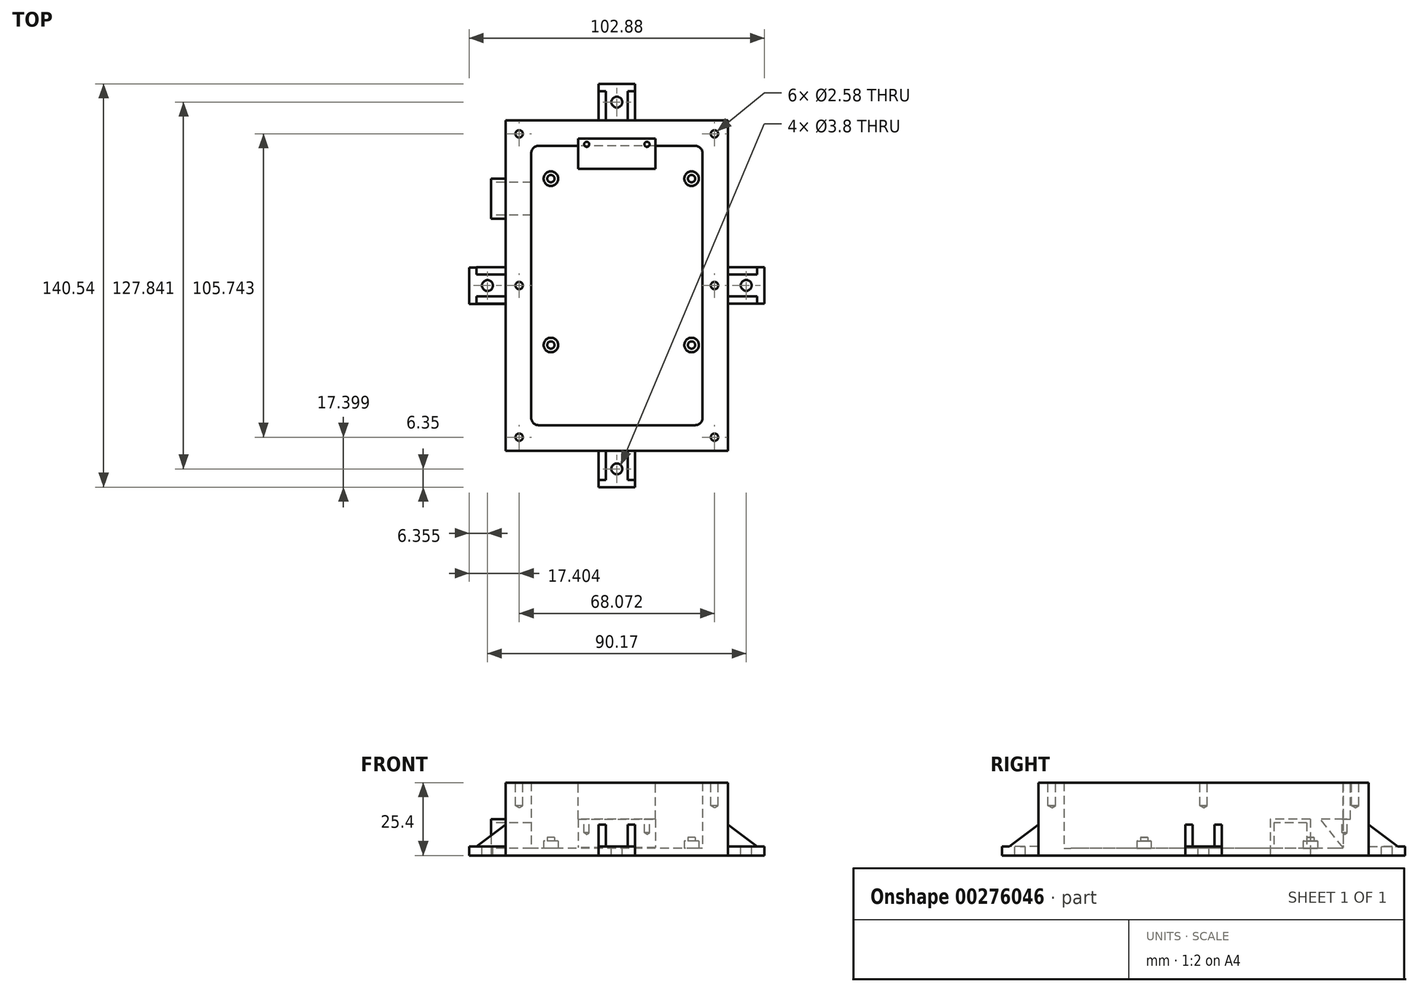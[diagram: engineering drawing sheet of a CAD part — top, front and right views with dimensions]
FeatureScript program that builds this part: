
annotation { "Feature Type Name" : "Feature", "Feature Type Description" : "" }
export const myFeature = defineFeature(function(context is Context, id is Id, definition is map)
    precondition{}
    {
        {
            var Q0;
            Q0=qCreatedBy(makeId("Top.planeOp"),FACE);
            var sketch = newSketch(context, id + "F0", { "sketchPlane" : qUnion([Q0])});
            skLineSegment(sketch, "E0.bottom", {"start": v(38.74, 57.57) * mm, "end": v(-38.74, 57.57) * mm});
            skLineSegment(sketch, "E0.top", {"start": v(38.74, -57.57) * mm, "end": v(-38.74, -57.57) * mm});
            skLineSegment(sketch, "E0.left", {"start": v(38.74, 57.57) * mm, "end": v(38.73, -57.57) * mm});
            skLineSegment(sketch, "E0.right", {"start": v(-38.73, 57.57) * mm, "end": v(-38.74, -57.57) * mm});
            skPoint(sketch, "E0.middle", {"position": v(0, 0) * mm});
            skLineSegment(sketch, "E1.bottom", {"start": v(27.3, 48.68) * mm, "end": v(-27.3, 48.68) * mm});
            skLineSegment(sketch, "E1.top", {"start": v(27.3, -48.68) * mm, "end": v(-27.3, -48.68) * mm});
            skLineSegment(sketch, "E1.left", {"start": v(29.85, 46.14) * mm, "end": v(29.84, -46.14) * mm});
            skLineSegment(sketch, "E1.right", {"start": v(-29.84, 46.14) * mm, "end": v(-29.85, -46.14) * mm});
            skPoint(sketch, "E2.visualSharp", {"position": v(-29.84, 48.68) * mm});
            skPoint(sketch, "E3.visualSharp", {"position": v(29.85, 48.68) * mm});
            skPoint(sketch, "E4.visualSharp", {"position": v(29.84, -48.68) * mm});
            skPoint(sketch, "E5.visualSharp", {"position": v(-29.85, -48.68) * mm});
            skArc(sketch, "E6.filletArc", {"start": v(29.85, 46.14) * mm, "mid": v(29.1, 47.94) * mm, "end": v(27.3, 48.68) * mm});
            skArc(sketch, "E7.filletArc", {"start": v(-27.3, 48.68) * mm, "mid": v(-29.1, 47.94) * mm, "end": v(-29.84, 46.14) * mm});
            skArc(sketch, "E8.filletArc", {"start": v(-29.85, -46.14) * mm, "mid": v(-29.1, -47.94) * mm, "end": v(-27.3, -48.68) * mm});
            skArc(sketch, "E9.filletArc", {"start": v(27.3, -48.68) * mm, "mid": v(29.1, -47.94) * mm, "end": v(29.84, -46.14) * mm});
            skSolve(sketch);
        }
        {
            var Q0;
            Q0=makeQuery(id+"F0.imprint","IMPRINT",FACE,{"disambiguationData":[TD([[makeQuery(id+"F0.imprint","IMPRINT",EDGE,{"derivedFrom":sQuery(id+"F0.wireOp",EDGE,"E0.bottom")}),1.0]])]});
            extrude(context, id + "F1", {"entities" : qUnion([Q0]), "depth" : 25.4 * mm});
        }
        {
            var Q0;
            Q0=makeQuery(id+"F0.imprint","IMPRINT",FACE,{"disambiguationData":[TD([[makeQuery(id+"F0.imprint","IMPRINT",EDGE,{"derivedFrom":sQuery(id+"F0.wireOp",EDGE,"E1.bottom")}),1.0]])]});
            extrude(context, id + "F2", {"entities" : qUnion([Q0]), "operationType" : NewBodyOperationType.ADD, "depth" : 2.54 * mm});
        }
        {
            var Q0;
            Q0=makeQuery(id+"F2.opExtrude","CAP_FACE",FACE,{"disambiguationData":[OSD([sQuery(id+"F0.wireOp",EDGE,"E1.bottom"),sQuery(id+"F0.wireOp",EDGE,"E1.top"),sQuery(id+"F0.wireOp",EDGE,"E1.left"),sQuery(id+"F0.wireOp",EDGE,"E1.right"),sQuery(id+"F0.wireOp",EDGE,"E2.filletArc"),sQuery(id+"F0.wireOp",EDGE,"E3.filletArc"),sQuery(id+"F0.wireOp",EDGE,"E4.filletArc"),sQuery(id+"F0.wireOp",EDGE,"E5.filletArc")])],"isStart":false});
            var sketch = newSketch(context, id + "F3", { "sketchPlane" : qUnion([Q0])});
            skCircle(sketch, "E10", {"center": v(-22.99, 37.25) * mm, "radius": 2.54 * mm});
            skCircle(sketch, "E11", {"center": v(26.04, 37.25) * mm, "radius": 2.54 * mm});
            skCircle(sketch, "E12", {"center": v(26.04, -20.74) * mm, "radius": 2.54 * mm});
            skCircle(sketch, "E13", {"center": v(-22.99, -20.74) * mm, "radius": 2.54 * mm});
            skSolve(sketch);
        }
        {
            var Q0;
            Q0 = qSketchRegion(id + "F3", true);
            extrude(context, id + "F4", {"entities" : qUnion([Q0]), "operationType" : NewBodyOperationType.ADD, "depth" : 2.54 * mm});
        }
        {
            var Q0;
            Q0=makeQuery(id+"F4.opExtrude","CAP_FACE",FACE,{"disambiguationData":[OSD([sQuery(id+"F3.wireOp",EDGE,"E10")])],"isStart":false});
            var sketch = newSketch(context, id + "F5", { "sketchPlane" : qUnion([Q0])});
            skCircle(sketch, "E14", {"center": v(26.04, 37.25) * mm, "radius": 1.27 * mm});
            skCircle(sketch, "E15", {"center": v(-22.99, 37.25) * mm, "radius": 1.27 * mm});
            skCircle(sketch, "E16", {"center": v(-22.99, -20.74) * mm, "radius": 1.27 * mm});
            skCircle(sketch, "E17", {"center": v(26.04, -20.74) * mm, "radius": 1.27 * mm});
            skSolve(sketch);
        }
        {
            var Q0;
            Q0=makeQuery(id+"F5.imprint","IMPRINT",FACE,{"disambiguationData":[TD([[makeQuery(id+"F5.imprint","IMPRINT",EDGE,{"derivedFrom":sQuery(id+"F5.wireOp",EDGE,"E15")}),1.0]])]});
            var Q1;
            Q1=makeQuery(id+"F5.imprint","IMPRINT",FACE,{"disambiguationData":[TD([[makeQuery(id+"F5.imprint","IMPRINT",EDGE,{"derivedFrom":sQuery(id+"F5.wireOp",EDGE,"E14")}),1.0]])]});
            var Q2;
            Q2=makeQuery(id+"F5.imprint","IMPRINT",FACE,{"disambiguationData":[TD([[makeQuery(id+"F5.imprint","IMPRINT",EDGE,{"derivedFrom":sQuery(id+"F5.wireOp",EDGE,"E17")}),1.0]])]});
            var Q3;
            Q3=makeQuery(id+"F5.imprint","IMPRINT",FACE,{"disambiguationData":[TD([[makeQuery(id+"F5.imprint","IMPRINT",EDGE,{"derivedFrom":sQuery(id+"F5.wireOp",EDGE,"E16")}),1.0]])]});
            extrude(context, id + "F6", {"entities" : qUnion([Q0, Q1, Q2, Q3]), "operationType" : NewBodyOperationType.ADD, "depth" : 1.27 * mm});
        }
        {
            var Q0;
            Q0=makeQuery(id+"F1.opExtrude","SWEPT_FACE",FACE,{"disambiguationData":[OSD([sQuery(id+"F0.wireOp",EDGE,"E0.right")])]});
            var sketch = newSketch(context, id + "F7", { "sketchPlane" : qUnion([Q0])});
            skLineSegment(sketch, "E18.bottom", {"start": v(-35.98, 11.43) * mm, "end": v(-24.55, 11.43) * mm});
            skLineSegment(sketch, "E18.top", {"start": v(-35.98, 2.54) * mm, "end": v(-24.55, 2.54) * mm});
            skLineSegment(sketch, "E18.left", {"start": v(-35.98, 11.43) * mm, "end": v(-35.98, 2.54) * mm});
            skLineSegment(sketch, "E18.right", {"start": v(-24.55, 11.43) * mm, "end": v(-24.55, 2.54) * mm});
            skLineSegment(sketch, "E19.bottom", {"start": v(-37.25, 12.7) * mm, "end": v(-23.28, 12.7) * mm});
            skLineSegment(sketch, "E19.top", {"start": v(-37.25, 0) * mm, "end": v(-23.28, 0) * mm});
            skLineSegment(sketch, "E19.left", {"start": v(-37.25, 12.7) * mm, "end": v(-37.25, 0) * mm});
            skLineSegment(sketch, "E19.right", {"start": v(-23.28, 12.7) * mm, "end": v(-23.28, 0) * mm});
            skSolve(sketch);
        }
        {
            var Q0;
            Q0=makeQuery(id+"F7.imprint","IMPRINT",FACE,{"disambiguationData":[TD([[makeQuery(id+"F7.imprint","IMPRINT",EDGE,{"derivedFrom":sQuery(id+"F7.wireOp",EDGE,"E18.bottom")}),-1.0]])]});
            extrude(context, id + "F8", {"entities" : qUnion([Q0]), "operationType" : NewBodyOperationType.REMOVE, "endBound" : BoundingType.UP_TO_NEXT, "oppositeDirection" : true, "depth" : 25.4 * mm});
        }
        {
            var Q0;
            Q0 = qSketchRegion(id + "F7", true);
            extrude(context, id + "F9", {"entities" : qUnion([Q0]), "operationType" : NewBodyOperationType.ADD, "depth" : 5.08 * mm});
        }
        {
            var Q0;
            Q0=makeQuery(id+"F1.opExtrude","CAP_FACE",FACE,{"disambiguationData":[OSD([sQuery(id+"F0.wireOp",EDGE,"E0.bottom"),sQuery(id+"F0.wireOp",EDGE,"E0.top"),sQuery(id+"F0.wireOp",EDGE,"E0.left"),sQuery(id+"F0.wireOp",EDGE,"E0.right"),sQuery(id+"F0.wireOp",EDGE,"E1.bottom"),sQuery(id+"F0.wireOp",EDGE,"E1.top"),sQuery(id+"F0.wireOp",EDGE,"E1.left"),sQuery(id+"F0.wireOp",EDGE,"E1.right"),sQuery(id+"F0.wireOp",EDGE,"E6.filletArc"),sQuery(id+"F0.wireOp",EDGE,"E7.filletArc"),sQuery(id+"F0.wireOp",EDGE,"E8.filletArc"),sQuery(id+"F0.wireOp",EDGE,"E9.filletArc")])],"isStart":false});
            var sketch = newSketch(context, id + "F10", { "sketchPlane" : qUnion([Q0])});
            skCircle(sketch, "E20", {"center": v(-34.04, 52.87) * mm, "radius": 1.27 * mm});
            skCircle(sketch, "E21", {"center": v(34.04, 52.87) * mm, "radius": 1.27 * mm});
            skCircle(sketch, "E22", {"center": v(-34.04, -52.87) * mm, "radius": 1.27 * mm});
            skCircle(sketch, "E23", {"center": v(34.04, -52.87) * mm, "radius": 1.27 * mm});
            skPoint(sketch, "E24", {"position": v(34.04, 0) * mm});
            skPoint(sketch, "E25", {"position": v(-34.04, 0) * mm});
            skPoint(sketch, "E25.positionSnap0", {"position": v(-38.73, 0) * mm});
            skSolve(sketch);
        }
        {
            var Q0;
            Q0=makeQuery(id+"F1.opExtrude","CAP_FACE",FACE,{"disambiguationData":[OSD([sQuery(id+"F0.wireOp",EDGE,"E0.bottom"),sQuery(id+"F0.wireOp",EDGE,"E0.top"),sQuery(id+"F0.wireOp",EDGE,"E0.left"),sQuery(id+"F0.wireOp",EDGE,"E0.right"),sQuery(id+"F0.wireOp",EDGE,"E1.bottom"),sQuery(id+"F0.wireOp",EDGE,"E1.top"),sQuery(id+"F0.wireOp",EDGE,"E1.left"),sQuery(id+"F0.wireOp",EDGE,"E1.right"),sQuery(id+"F0.wireOp",EDGE,"E6.filletArc"),sQuery(id+"F0.wireOp",EDGE,"E7.filletArc"),sQuery(id+"F0.wireOp",EDGE,"E8.filletArc"),sQuery(id+"F0.wireOp",EDGE,"E9.filletArc")])],"isStart":false});
            var sketch = newSketch(context, id + "F11", { "sketchPlane" : qUnion([Q0])});
            skLineSegment(sketch, "E26.bottom", {"start": v(-13.5, 48.68) * mm, "end": v(13.5, 48.68) * mm});
            skLineSegment(sketch, "E26.top", {"start": v(-13.5, 51.22) * mm, "end": v(13.5, 51.22) * mm});
            skLineSegment(sketch, "E26.left", {"start": v(-13.5, 48.68) * mm, "end": v(-13.5, 51.22) * mm});
            skLineSegment(sketch, "E26.right", {"start": v(13.5, 48.68) * mm, "end": v(13.5, 51.22) * mm});
            skLineSegment(sketch, "E27", {"start": v(-13.5, 48.68) * mm, "end": v(-13.5, 27.22) * mm});
            skLineSegment(sketch, "E28", {"start": v(-13.5, 27.22) * mm, "end": v(13.5, 27.22) * mm});
            skLineSegment(sketch, "E29", {"start": v(13.5, 27.22) * mm, "end": v(13.5, 48.68) * mm});
            skSolve(sketch);
        }
        {
            var Q0;
            Q0=makeQuery(id+"F11.imprint","IMPRINT",FACE,{"disambiguationData":[TD([[makeQuery(id+"F11.imprint","IMPRINT",EDGE,{"derivedFrom":sQuery(id+"F11.wireOp",EDGE,"E26.bottom")}),-1.0]])]});
            extrude(context, id + "F12", {"entities" : qUnion([Q0]), "operationType" : NewBodyOperationType.REMOVE, "oppositeDirection" : true, "depth" : 12.7 * mm});
        }
        {
            var Q0;
            Q0=makeQuery(id+"F12.boolean.opBoolean","COPY",FACE,{"derivedFrom":makeQuery(id+"F12.opExtrude","CAP_FACE",FACE,{"disambiguationData":[OSD([sQuery(id+"F11.wireOp",EDGE,"E26.bottom"),sQuery(id+"F11.wireOp",EDGE,"E26.top"),sQuery(id+"F11.wireOp",EDGE,"E26.left"),sQuery(id+"F11.wireOp",EDGE,"E26.right")])],"isStart":false})});
            var sketch = newSketch(context, id + "F13", { "sketchPlane" : qUnion([Q0])});
            skCircle(sketch, "E30", {"center": v(-10.5, 49.22) * mm, "radius": 1 * mm});
            skCircle(sketch, "E31", {"center": v(10.5, 49.22) * mm, "radius": 1 * mm});
            skSolve(sketch);
        }
        {
            var Q0;
            Q0=makeQuery(id+"F1.opExtrude","SWEPT_FACE",FACE,{"disambiguationData":[OSD([sQuery(id+"F0.wireOp",EDGE,"E0.top")])]});
            var sketch = newSketch(context, id + "F14", { "sketchPlane" : qUnion([Q0])});
            skLineSegment(sketch, "E32.bottom", {"start": v(-6.35, 0) * mm, "end": v(6.35, 0) * mm});
            skLineSegment(sketch, "E32.top", {"start": v(-6.35, 3.17) * mm, "end": v(6.35, 3.18) * mm});
            skLineSegment(sketch, "E32.left", {"start": v(-6.35, 0) * mm, "end": v(-6.35, 3.17) * mm});
            skLineSegment(sketch, "E32.right", {"start": v(6.35, 0) * mm, "end": v(6.35, 3.18) * mm});
            skSolve(sketch);
        }
        {
            var Q0;
            Q0=makeQuery(id+"F14.imprint","IMPRINT",FACE,{"disambiguationData":[TD([[makeQuery(id+"F14.imprint","IMPRINT",EDGE,{"derivedFrom":sQuery(id+"F14.wireOp",EDGE,"E32.bottom")}),-1.0]])]});
            extrude(context, id + "F15", {"entities" : qUnion([Q0]), "operationType" : NewBodyOperationType.ADD, "depth" : 12.7 * mm});
        }
        {
            var Q0;
            Q0=makeQuery(id+"F1.opExtrude","SWEPT_FACE",FACE,{"disambiguationData":[OSD([sQuery(id+"F0.wireOp",EDGE,"E0.bottom")])]});
            var sketch = newSketch(context, id + "F16", { "sketchPlane" : qUnion([Q0])});
            skLineSegment(sketch, "E33.bottom", {"start": v(-6.35, 0) * mm, "end": v(6.35, 0) * mm});
            skLineSegment(sketch, "E33.top", {"start": v(-6.35, 3.17) * mm, "end": v(6.35, 3.18) * mm});
            skLineSegment(sketch, "E33.left", {"start": v(-6.35, 0) * mm, "end": v(-6.35, 3.17) * mm});
            skLineSegment(sketch, "E33.right", {"start": v(6.35, 0) * mm, "end": v(6.35, 3.18) * mm});
            skSolve(sketch);
        }
        {
            var Q0;
            Q0 = qSketchRegion(id + "F16", true);
            extrude(context, id + "F17", {"entities" : qUnion([Q0]), "operationType" : NewBodyOperationType.ADD, "depth" : 12.7 * mm});
        }
        {
            var Q0;
            Q0=makeQuery(id+"F1.opExtrude","SWEPT_FACE",FACE,{"disambiguationData":[OSD([sQuery(id+"F0.wireOp",EDGE,"E0.left")])]});
            var sketch = newSketch(context, id + "F18", { "sketchPlane" : qUnion([Q0])});
            skLineSegment(sketch, "E34.bottom", {"start": v(-6.31, 0) * mm, "end": v(6.39, 0) * mm});
            skLineSegment(sketch, "E34.top", {"start": v(-6.31, 3.17) * mm, "end": v(6.39, 3.18) * mm});
            skLineSegment(sketch, "E34.left", {"start": v(-6.31, 0) * mm, "end": v(-6.31, 3.17) * mm});
            skLineSegment(sketch, "E34.right", {"start": v(6.39, 0) * mm, "end": v(6.39, 3.18) * mm});
            skSolve(sketch);
        }
        {
            var Q0;
            Q0 = qSketchRegion(id + "F18", true);
            extrude(context, id + "F19", {"entities" : qUnion([Q0]), "operationType" : NewBodyOperationType.ADD, "depth" : 12.7 * mm});
        }
        {
            var Q0;
            Q0=makeQuery(id+"F1.opExtrude","SWEPT_FACE",FACE,{"disambiguationData":[OSD([sQuery(id+"F0.wireOp",EDGE,"E0.right")])]});
            var sketch = newSketch(context, id + "F20", { "sketchPlane" : qUnion([Q0])});
            skLineSegment(sketch, "E35.bottom", {"start": v(-6.31, 0) * mm, "end": v(6.39, 0) * mm});
            skLineSegment(sketch, "E35.top", {"start": v(-6.31, 3.18) * mm, "end": v(6.39, 3.18) * mm});
            skLineSegment(sketch, "E35.left", {"start": v(-6.31, 0) * mm, "end": v(-6.31, 3.18) * mm});
            skLineSegment(sketch, "E35.right", {"start": v(6.39, 0) * mm, "end": v(6.39, 3.18) * mm});
            skSolve(sketch);
        }
        {
            var Q0;
            Q0 = qSketchRegion(id + "F20", true);
            extrude(context, id + "F21", {"entities" : qUnion([Q0]), "operationType" : NewBodyOperationType.ADD, "depth" : 12.7 * mm});
        }
        {
            var Q0;
            Q0=makeQuery(id+"F17.opExtrude","SWEPT_FACE",FACE,{"disambiguationData":[OSD([sQuery(id+"F16.wireOp",EDGE,"E33.top")])]});
            var sketch = newSketch(context, id + "F22", { "sketchPlane" : qUnion([Q0])});
            skPoint(sketch, "E36", {"position": v(0, 63.92) * mm});
            skSolve(sketch);
        }
        {
            var Q0;
            Q0=makeQuery(id+"F21.opExtrude","SWEPT_FACE",FACE,{"disambiguationData":[OSD([sQuery(id+"F20.wireOp",EDGE,"E35.top")])]});
            var sketch = newSketch(context, id + "F23", { "sketchPlane" : qUnion([Q0])});
            skPoint(sketch, "E37", {"position": v(-45.09, 0) * mm});
            skPoint(sketch, "E37.positionSnap0", {"position": v(-45.09, 6.31) * mm});
            skSolve(sketch);
        }
        {
            var Q0;
            Q0=makeQuery(id+"F19.opExtrude","SWEPT_FACE",FACE,{"disambiguationData":[OSD([sQuery(id+"F18.wireOp",EDGE,"E34.top")])]});
            var sketch = newSketch(context, id + "F24", { "sketchPlane" : qUnion([Q0])});
            skPoint(sketch, "E38", {"position": v(45.09, 0.04) * mm});
            skPoint(sketch, "E38.positionSnap0", {"position": v(45.09, 6.39) * mm});
            skPoint(sketch, "E38.positionSnap1", {"position": v(51.44, 0.04) * mm});
            skSolve(sketch);
        }
        {
            var Q0;
            Q0=makeQuery(id+"F15.opExtrude","SWEPT_FACE",FACE,{"disambiguationData":[OSD([sQuery(id+"F14.wireOp",EDGE,"E32.top")])]});
            var sketch = newSketch(context, id + "F25", { "sketchPlane" : qUnion([Q0])});
            skPoint(sketch, "E39", {"position": v(0, -63.92) * mm});
            skPoint(sketch, "E39.positionSnap0", {"position": v(0, -70.27) * mm});
            skSolve(sketch);
        }
        {
            var Q0;
            Q0=qCreatedBy(makeId("Right.planeOp"),FACE);
            var sketch = newSketch(context, id + "F26", { "sketchPlane" : qUnion([Q0])});
            skLineSegment(sketch, "E40", {"start": v(48.68, 12.7) * mm, "end": v(40.68, 12.7) * mm});
            skLineSegment(sketch, "E41", {"start": v(48.68, 12.7) * mm, "end": v(48.68, 2.7) * mm});
            skLineSegment(sketch, "E42", {"start": v(48.68, 2.7) * mm, "end": v(40.68, 12.7) * mm});
            skSolve(sketch);
        }
        {
            var Q0;
            Q0=makeQuery(id+"F26.imprint","IMPRINT",FACE,{"disambiguationData":[TD([[makeQuery(id+"F26.imprint","IMPRINT",EDGE,{"derivedFrom":sQuery(id+"F26.wireOp",EDGE,"E40")}),1.0]])]});
            extrude(context, id + "F27", {"entities" : qUnion([Q0]), "operationType" : NewBodyOperationType.ADD, "endBound" : BoundingType.SYMMETRIC, "depth" : 27 * mm});
        }
        {
            var Q0;
            Q0=sQuery(id+"F13.wireOp",VERTEX,"E30.center");
            var Q1;
            Q1=sQuery(id+"F13.wireOp",VERTEX,"E31.center");
            var Q2;
            Q2=makeQuery(id+"F1.opExtrude","SWEPT_BODY",BODY,{"disambiguationData":[OSD([sQuery(id+"F0.wireOp",EDGE,"E0.bottom"),sQuery(id+"F0.wireOp",EDGE,"E0.top"),sQuery(id+"F0.wireOp",EDGE,"E0.left"),sQuery(id+"F0.wireOp",EDGE,"E0.right"),sQuery(id+"F0.wireOp",EDGE,"E1.bottom"),sQuery(id+"F0.wireOp",EDGE,"E1.top"),sQuery(id+"F0.wireOp",EDGE,"E1.left"),sQuery(id+"F0.wireOp",EDGE,"E1.right"),sQuery(id+"F0.wireOp",EDGE,"E6.filletArc"),sQuery(id+"F0.wireOp",EDGE,"E7.filletArc"),sQuery(id+"F0.wireOp",EDGE,"E8.filletArc"),sQuery(id+"F0.wireOp",EDGE,"E9.filletArc")])]});
            hole(context, id + "F28", {"style" : HoleStyle.SIMPLE, "endStyle" : HoleEndStyle.BLIND, "standardTappedOrClearance" : lookupTablePath({ "standard" : "ANSI", "engagement" : "75%", "pitch" : "64 tpi", "size" : "#2", "type" : "Tapped" }), "standardBlindInLast" : lookupTablePath({ "standard" : "ANSI", "engagement" : "75%", "pitch" : "64 tpi", "size" : "#2", "type" : "Tapped" }), "holeDiameter" : 1.78 * mm, "showTappedDepth" : true, "holeDepth" : 4.8 * mm, "tappedDepth" : 4.8 * mm, "tapClearance" : 0, "locations" : qUnion([Q0, Q1]), "scope" : qUnion([Q2]), "majorDiameter" : 2.18 * mm});
        }
        {
            var Q0;
            Q0=sQuery(id+"F10.wireOp",VERTEX,"E20.center");
            var Q1;
            Q1=sQuery(id+"F10.wireOp",VERTEX,"E21.center");
            var Q2;
            Q2=sQuery(id+"F10.wireOp",VERTEX,"E23.center");
            var Q3;
            Q3=sQuery(id+"F10.wireOp",VERTEX,"E22.center");
            var Q4;
            Q4=sQuery(id+"F10.wireOp",VERTEX,"E24");
            var Q5;
            Q5=sQuery(id+"F10.wireOp",VERTEX,"E25");
            var Q6;
            Q6=makeQuery(id+"F1.opExtrude","SWEPT_BODY",BODY,{"disambiguationData":[OSD([sQuery(id+"F0.wireOp",EDGE,"E0.bottom"),sQuery(id+"F0.wireOp",EDGE,"E0.top"),sQuery(id+"F0.wireOp",EDGE,"E0.left"),sQuery(id+"F0.wireOp",EDGE,"E0.right"),sQuery(id+"F0.wireOp",EDGE,"E1.bottom"),sQuery(id+"F0.wireOp",EDGE,"E1.top"),sQuery(id+"F0.wireOp",EDGE,"E1.left"),sQuery(id+"F0.wireOp",EDGE,"E1.right"),sQuery(id+"F0.wireOp",EDGE,"E6.filletArc"),sQuery(id+"F0.wireOp",EDGE,"E7.filletArc"),sQuery(id+"F0.wireOp",EDGE,"E8.filletArc"),sQuery(id+"F0.wireOp",EDGE,"E9.filletArc")])]});
            hole(context, id + "F29", {"style" : HoleStyle.SIMPLE, "endStyle" : HoleEndStyle.BLIND, "standardTappedOrClearance" : lookupTablePath({ "standard" : "ANSI", "engagement" : "75%", "pitch" : "40 tpi", "size" : "#5", "type" : "Tapped" }), "standardBlindInLast" : lookupTablePath({ "standard" : "ANSI", "engagement" : "75%", "pitch" : "40 tpi", "size" : "#5", "type" : "Tapped" }), "holeDiameter" : 2.58 * mm, "showTappedDepth" : true, "holeDepth" : 8 * mm, "tappedDepth" : 8 * mm, "tapClearance" : 0, "locations" : qUnion([Q0, Q1, Q2, Q3, Q4, Q5]), "scope" : qUnion([Q6]), "majorDiameter" : 3.18 * mm});
        }
        {
            var Q0;
            Q0=sQuery(id+"F22.wireOp",VERTEX,"E36");
            var Q1;
            Q1=sQuery(id+"F24.wireOp",VERTEX,"E38");
            var Q2;
            Q2=sQuery(id+"F23.wireOp",VERTEX,"E37");
            var Q3;
            Q3=sQuery(id+"F25.wireOp",VERTEX,"E39");
            var Q4;
            Q4=makeQuery(id+"F1.opExtrude","SWEPT_BODY",BODY,{"disambiguationData":[OSD([sQuery(id+"F0.wireOp",EDGE,"E0.bottom"),sQuery(id+"F0.wireOp",EDGE,"E0.top"),sQuery(id+"F0.wireOp",EDGE,"E0.left"),sQuery(id+"F0.wireOp",EDGE,"E0.right"),sQuery(id+"F0.wireOp",EDGE,"E1.bottom"),sQuery(id+"F0.wireOp",EDGE,"E1.top"),sQuery(id+"F0.wireOp",EDGE,"E1.left"),sQuery(id+"F0.wireOp",EDGE,"E1.right"),sQuery(id+"F0.wireOp",EDGE,"E6.filletArc"),sQuery(id+"F0.wireOp",EDGE,"E7.filletArc"),sQuery(id+"F0.wireOp",EDGE,"E8.filletArc"),sQuery(id+"F0.wireOp",EDGE,"E9.filletArc")])]});
            hole(context, id + "F30", {"style" : HoleStyle.SIMPLE, "endStyle" : HoleEndStyle.THROUGH, "standardTappedOrClearance" : lookupTablePath({ "standard" : "ANSI", "fit" : "Normal (ASME)", "size" : "#6", "type" : "Clearance" }), "standardBlindInLast" : lookupTablePath({ "fit" : "Free", "standard" : "ANSI", "size" : "#6", "type" : "Clearance" }), "holeDiameter" : 3.8 * mm, "tappedDepth" : 4.8 * mm, "tapClearance" : 0, "locations" : qUnion([Q0, Q1, Q2, Q3]), "scope" : qUnion([Q4])});
        }
        {
            var Q0;
            Q0=qCreatedBy(makeId("Right.planeOp"),FACE);
            var sketch = newSketch(context, id + "F31", { "sketchPlane" : qUnion([Q0])});
            skLineSegment(sketch, "E43", {"start": v(57.57, 10.8) * mm, "end": v(57.57, 3.17) * mm});
            skLineSegment(sketch, "E44", {"start": v(57.57, 3.17) * mm, "end": v(67.73, 3.18) * mm});
            skLineSegment(sketch, "E45", {"start": v(67.73, 3.18) * mm, "end": v(57.57, 10.8) * mm});
            skSolve(sketch);
        }
        {
            var Q0;
            Q0=makeQuery(id+"F31.imprint","IMPRINT",FACE,{"disambiguationData":[TD([[makeQuery(id+"F31.imprint","IMPRINT",EDGE,{"derivedFrom":sQuery(id+"F31.wireOp",EDGE,"E43")}),1.0]])]});
            extrude(context, id + "F32", {"entities" : qUnion([Q0]), "operationType" : NewBodyOperationType.ADD, "endBound" : BoundingType.SYMMETRIC, "depth" : 12.7 * mm});
        }
        {
            var Q0;
            Q0 = qSketchRegion(id + "F31", true);
            extrude(context, id + "F33", {"entities" : qUnion([Q0]), "operationType" : NewBodyOperationType.REMOVE, "endBound" : BoundingType.SYMMETRIC, "oppositeDirection" : true, "depth" : 7.62 * mm});
        }
        {
            var Q0;
            Q0=qCreatedBy(makeId("Front.planeOp"),FACE);
            var sketch = newSketch(context, id + "F34", { "sketchPlane" : qUnion([Q0])});
            skLineSegment(sketch, "E46", {"start": v(38.73, 10.8) * mm, "end": v(38.73, 3.17) * mm});
            skLineSegment(sketch, "E47", {"start": v(38.73, 3.17) * mm, "end": v(48.9, 3.18) * mm});
            skLineSegment(sketch, "E48", {"start": v(48.9, 3.18) * mm, "end": v(38.73, 10.8) * mm});
            skSolve(sketch);
        }
        {
            var Q0;
            Q0=makeQuery(id+"F34.imprint","IMPRINT",FACE,{"disambiguationData":[TD([[makeQuery(id+"F34.imprint","IMPRINT",EDGE,{"derivedFrom":sQuery(id+"F34.wireOp",EDGE,"E46")}),1.0]])]});
            extrude(context, id + "F35", {"entities" : qUnion([Q0]), "operationType" : NewBodyOperationType.ADD, "endBound" : BoundingType.SYMMETRIC, "depth" : 12.7 * mm});
        }
        {
            var Q0;
            Q0 = qSketchRegion(id + "F34", true);
            extrude(context, id + "F36", {"entities" : qUnion([Q0]), "operationType" : NewBodyOperationType.REMOVE, "endBound" : BoundingType.SYMMETRIC, "oppositeDirection" : true, "depth" : 7.62 * mm});
        }
        {
            var Q0;
            Q0=qCreatedBy(makeId("Right.planeOp"),FACE);
            var sketch = newSketch(context, id + "F37", { "sketchPlane" : qUnion([Q0])});
            skLineSegment(sketch, "E49", {"start": v(-57.57, 10.8) * mm, "end": v(-57.57, 3.18) * mm});
            skLineSegment(sketch, "E50", {"start": v(-57.57, 3.17) * mm, "end": v(-67.73, 3.17) * mm});
            skLineSegment(sketch, "E51", {"start": v(-67.73, 3.17) * mm, "end": v(-57.57, 10.8) * mm});
            skSolve(sketch);
        }
        {
            var Q0;
            Q0=makeQuery(id+"F37.imprint","IMPRINT",FACE,{"disambiguationData":[TD([[makeQuery(id+"F37.imprint","IMPRINT",EDGE,{"derivedFrom":sQuery(id+"F37.wireOp",EDGE,"E49")}),-1.0]])]});
            extrude(context, id + "F38", {"entities" : qUnion([Q0]), "operationType" : NewBodyOperationType.ADD, "endBound" : BoundingType.SYMMETRIC, "depth" : 12.7 * mm});
        }
        {
            var Q0;
            Q0 = qSketchRegion(id + "F37", true);
            extrude(context, id + "F39", {"entities" : qUnion([Q0]), "operationType" : NewBodyOperationType.REMOVE, "endBound" : BoundingType.SYMMETRIC, "oppositeDirection" : true, "depth" : 7.62 * mm});
        }
        {
            var Q0;
            Q0=qCreatedBy(makeId("Front.planeOp"),FACE);
            var sketch = newSketch(context, id + "F40", { "sketchPlane" : qUnion([Q0])});
            skLineSegment(sketch, "E52", {"start": v(-38.74, 10.8) * mm, "end": v(-38.74, 3.18) * mm});
            skLineSegment(sketch, "E53", {"start": v(-38.74, 3.18) * mm, "end": v(-48.9, 3.17) * mm});
            skLineSegment(sketch, "E54", {"start": v(-48.9, 3.17) * mm, "end": v(-38.74, 10.8) * mm});
            skSolve(sketch);
        }
        {
            var Q0;
            Q0=makeQuery(id+"F40.imprint","IMPRINT",FACE,{"disambiguationData":[TD([[makeQuery(id+"F40.imprint","IMPRINT",EDGE,{"derivedFrom":sQuery(id+"F40.wireOp",EDGE,"E52")}),-1.0]])]});
            extrude(context, id + "F41", {"entities" : qUnion([Q0]), "operationType" : NewBodyOperationType.ADD, "endBound" : BoundingType.SYMMETRIC, "depth" : 12.7 * mm});
        }
        {
            var Q0;
            Q0 = qSketchRegion(id + "F40", true);
            extrude(context, id + "F42", {"entities" : qUnion([Q0]), "operationType" : NewBodyOperationType.REMOVE, "endBound" : BoundingType.SYMMETRIC, "oppositeDirection" : true, "depth" : 7.62 * mm});
        }
    });
